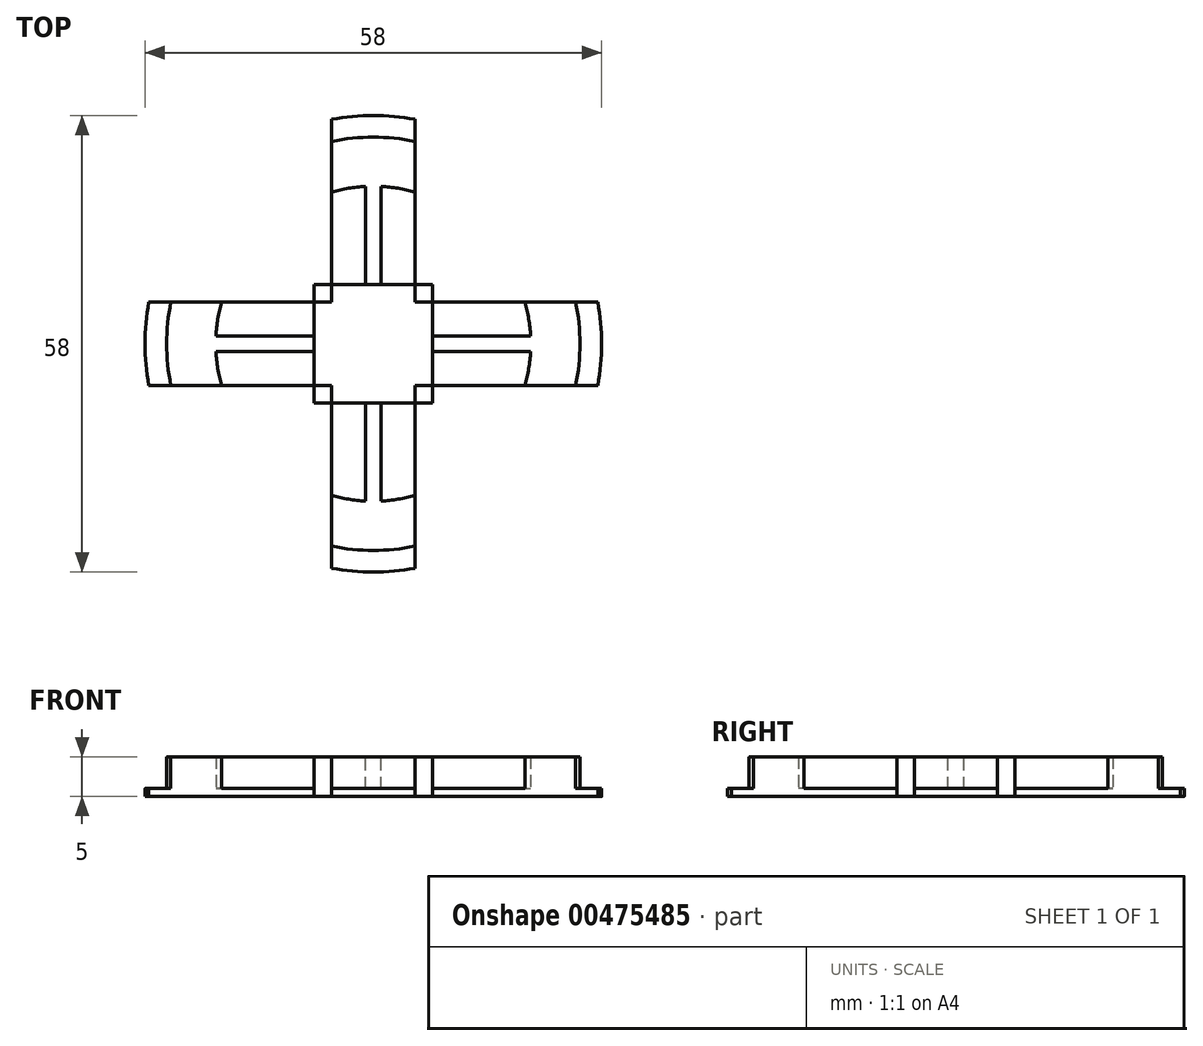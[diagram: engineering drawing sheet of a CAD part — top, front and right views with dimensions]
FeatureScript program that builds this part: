
annotation { "Feature Type Name" : "Feature", "Feature Type Description" : "" }
export const myFeature = defineFeature(function(context is Context, id is Id, definition is map)
    precondition{}
    {
        {
            var Q0;
            Q0=qCreatedBy(makeId("Top.planeOp"),FACE);
            var sketch = newSketch(context, id + "F0", { "sketchPlane" : qUnion([Q0])});
            skCircle(sketch, "E0", {"center": v(0, 0) * mm, "radius": 26.25 * mm});
            skCircle(sketch, "E1", {"center": v(0, 0) * mm, "radius": 29 * mm});
            skLineSegment(sketch, "E2.left", {"start": v(-5.27, 28.52) * mm, "end": v(-5.27, 5.27) * mm});
            skLineSegment(sketch, "E2.right", {"start": v(5.27, 28.52) * mm, "end": v(5.27, 5.27) * mm});
            skLineSegment(sketch, "E3.bottom", {"start": v(-28.52, 5.27) * mm, "end": v(-5.27, 5.27) * mm});
            skLineSegment(sketch, "E3.top", {"start": v(-28.52, -5.27) * mm, "end": v(-5.27, -5.27) * mm});
            skLineSegment(sketch, "E4.trimOffspring", {"start": v(5.27, 5.27) * mm, "end": v(28.52, 5.27) * mm});
            skLineSegment(sketch, "E5.trimOffspring", {"start": v(-5.27, -5.27) * mm, "end": v(-5.27, -28.52) * mm});
            skLineSegment(sketch, "E6.trimOffspring", {"start": v(5.27, -5.27) * mm, "end": v(28.52, -5.27) * mm});
            skLineSegment(sketch, "E7.trimOffspring", {"start": v(5.27, -5.27) * mm, "end": v(5.27, -28.52) * mm});
            skCircle(sketch, "E8", {"center": v(0, 0) * mm, "radius": 20 * mm});
            skCircle(sketch, "E9", {"center": v(0, 0) * mm, "radius": 4.1 * mm});
            skLineSegment(sketch, "E10.bottom", {"start": v(-7.5, 7.5) * mm, "end": v(7.5, 7.5) * mm});
            skLineSegment(sketch, "E10.top", {"start": v(-7.5, -7.5) * mm, "end": v(7.5, -7.5) * mm});
            skLineSegment(sketch, "E10.left", {"start": v(-7.5, 7.5) * mm, "end": v(-7.5, -7.5) * mm});
            skLineSegment(sketch, "E10.right", {"start": v(7.5, 7.5) * mm, "end": v(7.5, -7.5) * mm});
            skLineSegment(sketch, "E11.left", {"start": v(-1, 19.97) * mm, "end": v(-1, 7.5) * mm});
            skLineSegment(sketch, "E11.right", {"start": v(1, 19.97) * mm, "end": v(1, 7.5) * mm});
            skLineSegment(sketch, "E12.trimOffspring", {"start": v(-1, -7.5) * mm, "end": v(-1, -19.97) * mm});
            skLineSegment(sketch, "E13.trimOffspring", {"start": v(1, -7.5) * mm, "end": v(1, -19.97) * mm});
            skLineSegment(sketch, "E14.bottom", {"start": v(-19.97, 1) * mm, "end": v(-7.5, 1) * mm});
            skLineSegment(sketch, "E14.top", {"start": v(-19.97, -1) * mm, "end": v(-7.5, -1) * mm});
            skLineSegment(sketch, "E15.bottom", {"start": v(7.5, 1) * mm, "end": v(19.97, 1) * mm});
            skLineSegment(sketch, "E15.top", {"start": v(7.5, -1) * mm, "end": v(19.97, -1) * mm});
            skPoint(sketch, "E15.left.start.orphan", {"position": v(6.8, 1) * mm});
            skPoint(sketch, "E16.orphan", {"position": v(21.24, -1) * mm});
            skSolve(sketch);
        }
        {
            var Q0;
            {var subQ3=sQuery(id+"F0.wireOp",EDGE,"E0");var subQ9=sQuery(id+"F0.wireOp",EDGE,"E2.right");var subQ12=makeQuery(id+"F0.imprint","INTERSECT",VERTEX,{"derivedFrom":[subQ3,subQ9]});Q0=makeQuery(id+"F0.imprint","IMPRINT",FACE,{"disambiguationData":[TD([[makeQuery(id+"F0.imprint","IMPRINT",EDGE,{"disambiguationData":[TD([[subQ12,-1.0]])],"derivedFrom":subQ3}),1.0]])]});}
            var Q1;
            {var subQ0=sQuery(id+"F0.wireOp",EDGE,"E3.bottom");var subQ1=sQuery(id+"F0.wireOp",EDGE,"E0");var subQ2=makeQuery(id+"F0.imprint","INTERSECT",VERTEX,{"derivedFrom":[subQ1,subQ0]});Q1=makeQuery(id+"F0.imprint","IMPRINT",FACE,{"disambiguationData":[TD([[makeQuery(id+"F0.imprint","IMPRINT",EDGE,{"disambiguationData":[TD([[subQ2,-1.0]])],"derivedFrom":subQ1}),-1.0]])]});}
            var Q2;
            {var subQ0=sQuery(id+"F0.wireOp",EDGE,"E2.right");var subQ1=sQuery(id+"F0.wireOp",EDGE,"E0");var subQ2=makeQuery(id+"F0.imprint","INTERSECT",VERTEX,{"derivedFrom":[subQ1,subQ0]});Q2=makeQuery(id+"F0.imprint","IMPRINT",FACE,{"disambiguationData":[TD([[makeQuery(id+"F0.imprint","IMPRINT",EDGE,{"disambiguationData":[TD([[subQ2,-1.0]])],"derivedFrom":subQ1}),-1.0]])]});}
            var Q3;
            {var subQ0=sQuery(id+"F0.wireOp",EDGE,"E4.trimOffspring");var subQ1=sQuery(id+"F0.wireOp",EDGE,"E0");var subQ2=makeQuery(id+"F0.imprint","INTERSECT",VERTEX,{"derivedFrom":[subQ1,subQ0]});Q3=makeQuery(id+"F0.imprint","IMPRINT",FACE,{"disambiguationData":[TD([[makeQuery(id+"F0.imprint","IMPRINT",EDGE,{"disambiguationData":[TD([[subQ2,1.0]])],"derivedFrom":subQ1}),-1.0]])]});}
            var Q4;
            {var subQ0=sQuery(id+"F0.wireOp",EDGE,"E5.trimOffspring");var subQ1=sQuery(id+"F0.wireOp",EDGE,"E0");var subQ2=makeQuery(id+"F0.imprint","INTERSECT",VERTEX,{"derivedFrom":[subQ1,subQ0]});Q4=makeQuery(id+"F0.imprint","IMPRINT",FACE,{"disambiguationData":[TD([[makeQuery(id+"F0.imprint","IMPRINT",EDGE,{"disambiguationData":[TD([[subQ2,-1.0]])],"derivedFrom":subQ1}),-1.0]])]});}
            var Q5;
            {var subQ1=sQuery(id+"F0.wireOp",EDGE,"E3.bottom");var subQ3=sQuery(id+"F0.wireOp",EDGE,"E8");var subQ4=makeQuery(id+"F0.imprint","INTERSECT",VERTEX,{"derivedFrom":[subQ1,subQ3]});Q5=makeQuery(id+"F0.imprint","IMPRINT",FACE,{"disambiguationData":[TD([[makeQuery(id+"F0.imprint","IMPRINT",EDGE,{"disambiguationData":[TD([[subQ4,-1.0]])],"derivedFrom":subQ3}),1.0]])]});}
            var Q6;
            Q6=makeQuery(id+"F0.imprint","IMPRINT",FACE,{"disambiguationData":[TD([[makeQuery(id+"F0.imprint","IMPRINT",EDGE,{"derivedFrom":sQuery(id+"F0.wireOp",EDGE,"E9")}),-1.0]])]});
            var Q7;
            {var subQ1=sQuery(id+"F0.wireOp",EDGE,"E2.left");var subQ3=sQuery(id+"F0.wireOp",EDGE,"E8");var subQ4=makeQuery(id+"F0.imprint","INTERSECT",VERTEX,{"derivedFrom":[subQ1,subQ3]});Q7=makeQuery(id+"F0.imprint","IMPRINT",FACE,{"disambiguationData":[TD([[makeQuery(id+"F0.imprint","IMPRINT",EDGE,{"disambiguationData":[TD([[subQ4,1.0]])],"derivedFrom":subQ3}),1.0]])]});}
            var Q8;
            {var subQ1=sQuery(id+"F0.wireOp",EDGE,"E4.trimOffspring");var subQ3=sQuery(id+"F0.wireOp",EDGE,"E8");var subQ4=makeQuery(id+"F0.imprint","INTERSECT",VERTEX,{"derivedFrom":[subQ1,subQ3]});Q8=makeQuery(id+"F0.imprint","IMPRINT",FACE,{"disambiguationData":[TD([[makeQuery(id+"F0.imprint","IMPRINT",EDGE,{"disambiguationData":[TD([[subQ4,1.0]])],"derivedFrom":subQ3}),1.0]])]});}
            var Q9;
            {var subQ0=sQuery(id+"F0.wireOp",EDGE,"E4.trimOffspring");var subQ1=sQuery(id+"F0.wireOp",EDGE,"E0");var subQ2=makeQuery(id+"F0.imprint","INTERSECT",VERTEX,{"derivedFrom":[subQ1,subQ0]});Q9=makeQuery(id+"F0.imprint","IMPRINT",FACE,{"disambiguationData":[TD([[makeQuery(id+"F0.imprint","IMPRINT",EDGE,{"disambiguationData":[TD([[subQ2,1.0]])],"derivedFrom":subQ1}),1.0]])]});}
            var Q10;
            {var subQ1=sQuery(id+"F0.wireOp",EDGE,"E5.trimOffspring");var subQ3=sQuery(id+"F0.wireOp",EDGE,"E8");var subQ4=makeQuery(id+"F0.imprint","INTERSECT",VERTEX,{"derivedFrom":[subQ1,subQ3]});Q10=makeQuery(id+"F0.imprint","IMPRINT",FACE,{"disambiguationData":[TD([[makeQuery(id+"F0.imprint","IMPRINT",EDGE,{"disambiguationData":[TD([[subQ4,-1.0]])],"derivedFrom":subQ3}),1.0]])]});}
            var Q11;
            {var subQ0=sQuery(id+"F0.wireOp",EDGE,"E5.trimOffspring");var subQ1=sQuery(id+"F0.wireOp",EDGE,"E0");var subQ2=makeQuery(id+"F0.imprint","INTERSECT",VERTEX,{"derivedFrom":[subQ1,subQ0]});Q11=makeQuery(id+"F0.imprint","IMPRINT",FACE,{"disambiguationData":[TD([[makeQuery(id+"F0.imprint","IMPRINT",EDGE,{"disambiguationData":[TD([[subQ2,-1.0]])],"derivedFrom":subQ1}),1.0]])]});}
            var Q12;
            {var subQ0=sQuery(id+"F0.wireOp",EDGE,"E3.bottom");var subQ1=sQuery(id+"F0.wireOp",EDGE,"E0");var subQ2=makeQuery(id+"F0.imprint","INTERSECT",VERTEX,{"derivedFrom":[subQ1,subQ0]});Q12=makeQuery(id+"F0.imprint","IMPRINT",FACE,{"disambiguationData":[TD([[makeQuery(id+"F0.imprint","IMPRINT",EDGE,{"disambiguationData":[TD([[subQ2,-1.0]])],"derivedFrom":subQ1}),1.0]])]});}
            var Q13;
            {var subQ0=sQuery(id+"F0.wireOp",EDGE,"E3.bottom");var subQ1=sQuery(id+"F0.wireOp",EDGE,"E2.left");var subQ2=makeQuery(id+"F0.imprint","INTERSECT",VERTEX,{"derivedFrom":[subQ1,subQ0]});Q13=makeQuery(id+"F0.imprint","IMPRINT",FACE,{"disambiguationData":[TD([[makeQuery(id+"F0.imprint","IMPRINT",EDGE,{"disambiguationData":[TD([[subQ2,1.0]])],"derivedFrom":subQ1}),-1.0]])]});}
            var Q14;
            {var subQ0=sQuery(id+"F0.wireOp",EDGE,"E5.trimOffspring");var subQ1=sQuery(id+"F0.wireOp",EDGE,"E3.top");var subQ2=makeQuery(id+"F0.imprint","INTERSECT",VERTEX,{"derivedFrom":[subQ1,subQ0]});Q14=makeQuery(id+"F0.imprint","IMPRINT",FACE,{"disambiguationData":[TD([[makeQuery(id+"F0.imprint","IMPRINT",EDGE,{"disambiguationData":[TD([[subQ2,1.0]])],"derivedFrom":subQ1}),-1.0]])]});}
            var Q15;
            {var subQ0=sQuery(id+"F0.wireOp",EDGE,"E7.trimOffspring");var subQ1=sQuery(id+"F0.wireOp",EDGE,"E6.trimOffspring");var subQ2=makeQuery(id+"F0.imprint","INTERSECT",VERTEX,{"derivedFrom":[subQ1,subQ0]});Q15=makeQuery(id+"F0.imprint","IMPRINT",FACE,{"disambiguationData":[TD([[makeQuery(id+"F0.imprint","IMPRINT",EDGE,{"disambiguationData":[TD([[subQ2,-1.0]])],"derivedFrom":subQ1}),-1.0]])]});}
            var Q16;
            {var subQ0=sQuery(id+"F0.wireOp",EDGE,"E4.trimOffspring");var subQ1=sQuery(id+"F0.wireOp",EDGE,"E2.right");var subQ2=makeQuery(id+"F0.imprint","INTERSECT",VERTEX,{"derivedFrom":[subQ1,subQ0]});Q16=makeQuery(id+"F0.imprint","IMPRINT",FACE,{"disambiguationData":[TD([[makeQuery(id+"F0.imprint","IMPRINT",EDGE,{"disambiguationData":[TD([[subQ2,1.0]])],"derivedFrom":subQ1}),1.0]])]});}
            var Q17;
            {var subQ0=sQuery(id+"F0.wireOp",EDGE,"E15.bottom");Q17=makeQuery(id+"F0.imprint","IMPRINT",FACE,{"disambiguationData":[TD([[makeQuery(id+"F0.imprint","IMPRINT",EDGE,{"derivedFrom":subQ0}),-1.0]])]});}
            var Q18;
            {var subQ5=sQuery(id+"F0.wireOp",EDGE,"E15.top");Q18=makeQuery(id+"F0.imprint","IMPRINT",FACE,{"disambiguationData":[TD([[makeQuery(id+"F0.imprint","IMPRINT",EDGE,{"derivedFrom":subQ5}),-1.0]])]});}
            var Q19;
            {var subQ5=sQuery(id+"F0.wireOp",EDGE,"E14.top");Q19=makeQuery(id+"F0.imprint","IMPRINT",FACE,{"disambiguationData":[TD([[makeQuery(id+"F0.imprint","IMPRINT",EDGE,{"derivedFrom":subQ5}),-1.0]])]});}
            var Q20;
            {var subQ0=sQuery(id+"F0.wireOp",EDGE,"E14.bottom");Q20=makeQuery(id+"F0.imprint","IMPRINT",FACE,{"disambiguationData":[TD([[makeQuery(id+"F0.imprint","IMPRINT",EDGE,{"derivedFrom":subQ0}),-1.0]])]});}
            var Q21;
            {var subQ0=sQuery(id+"F0.wireOp",EDGE,"E11.left");Q21=makeQuery(id+"F0.imprint","IMPRINT",FACE,{"disambiguationData":[TD([[makeQuery(id+"F0.imprint","IMPRINT",EDGE,{"derivedFrom":subQ0}),1.0]])]});}
            var Q22;
            {var subQ5=sQuery(id+"F0.wireOp",EDGE,"E11.right");Q22=makeQuery(id+"F0.imprint","IMPRINT",FACE,{"disambiguationData":[TD([[makeQuery(id+"F0.imprint","IMPRINT",EDGE,{"derivedFrom":subQ5}),1.0]])]});}
            var Q23;
            {var subQ5=sQuery(id+"F0.wireOp",EDGE,"E13.trimOffspring");Q23=makeQuery(id+"F0.imprint","IMPRINT",FACE,{"disambiguationData":[TD([[makeQuery(id+"F0.imprint","IMPRINT",EDGE,{"derivedFrom":subQ5}),1.0]])]});}
            var Q24;
            {var subQ0=sQuery(id+"F0.wireOp",EDGE,"E12.trimOffspring");Q24=makeQuery(id+"F0.imprint","IMPRINT",FACE,{"disambiguationData":[TD([[makeQuery(id+"F0.imprint","IMPRINT",EDGE,{"derivedFrom":subQ0}),1.0]])]});}
            extrude(context, id + "F1", {"entities" : qUnion([Q0, Q1, Q2, Q3, Q4, Q5, Q6, Q7, Q8, Q9, Q10, Q11, Q12, Q13, Q14, Q15, Q16, Q17, Q18, Q19, Q20, Q21, Q22, Q23, Q24]), "oppositeDirection" : true, "depth" : 1 * mm, "offsetDistance" : 25 * mm});
        }
        {
            var Q0;
            {var subQ0=sQuery(id+"F0.wireOp",EDGE,"E4.trimOffspring");var subQ1=sQuery(id+"F0.wireOp",EDGE,"E0");var subQ2=makeQuery(id+"F0.imprint","INTERSECT",VERTEX,{"derivedFrom":[subQ1,subQ0]});Q0=makeQuery(id+"F0.imprint","IMPRINT",FACE,{"disambiguationData":[TD([[makeQuery(id+"F0.imprint","IMPRINT",EDGE,{"disambiguationData":[TD([[subQ2,1.0]])],"derivedFrom":subQ1}),1.0]])]});}
            var Q1;
            {var subQ0=sQuery(id+"F0.wireOp",EDGE,"E2.right");var subQ1=sQuery(id+"F0.wireOp",EDGE,"E0");var subQ2=makeQuery(id+"F0.imprint","INTERSECT",VERTEX,{"derivedFrom":[subQ1,subQ0]});Q1=makeQuery(id+"F0.imprint","IMPRINT",FACE,{"disambiguationData":[TD([[makeQuery(id+"F0.imprint","IMPRINT",EDGE,{"disambiguationData":[TD([[subQ2,-1.0]])],"derivedFrom":subQ1}),1.0]])]});}
            var Q2;
            {var subQ0=sQuery(id+"F0.wireOp",EDGE,"E3.bottom");var subQ1=sQuery(id+"F0.wireOp",EDGE,"E0");var subQ2=makeQuery(id+"F0.imprint","INTERSECT",VERTEX,{"derivedFrom":[subQ1,subQ0]});Q2=makeQuery(id+"F0.imprint","IMPRINT",FACE,{"disambiguationData":[TD([[makeQuery(id+"F0.imprint","IMPRINT",EDGE,{"disambiguationData":[TD([[subQ2,-1.0]])],"derivedFrom":subQ1}),1.0]])]});}
            var Q3;
            {var subQ0=sQuery(id+"F0.wireOp",EDGE,"E5.trimOffspring");var subQ1=sQuery(id+"F0.wireOp",EDGE,"E0");var subQ2=makeQuery(id+"F0.imprint","INTERSECT",VERTEX,{"derivedFrom":[subQ1,subQ0]});Q3=makeQuery(id+"F0.imprint","IMPRINT",FACE,{"disambiguationData":[TD([[makeQuery(id+"F0.imprint","IMPRINT",EDGE,{"disambiguationData":[TD([[subQ2,-1.0]])],"derivedFrom":subQ1}),1.0]])]});}
            var Q4;
            {var subQ0=sQuery(id+"F0.wireOp",EDGE,"E11.left");Q4=makeQuery(id+"F0.imprint","IMPRINT",FACE,{"disambiguationData":[TD([[makeQuery(id+"F0.imprint","IMPRINT",EDGE,{"derivedFrom":subQ0}),1.0]])]});}
            var Q5;
            {var subQ0=sQuery(id+"F0.wireOp",EDGE,"E14.bottom");Q5=makeQuery(id+"F0.imprint","IMPRINT",FACE,{"disambiguationData":[TD([[makeQuery(id+"F0.imprint","IMPRINT",EDGE,{"derivedFrom":subQ0}),-1.0]])]});}
            var Q6;
            {var subQ0=sQuery(id+"F0.wireOp",EDGE,"E15.bottom");Q6=makeQuery(id+"F0.imprint","IMPRINT",FACE,{"disambiguationData":[TD([[makeQuery(id+"F0.imprint","IMPRINT",EDGE,{"derivedFrom":subQ0}),-1.0]])]});}
            var Q7;
            {var subQ0=sQuery(id+"F0.wireOp",EDGE,"E12.trimOffspring");Q7=makeQuery(id+"F0.imprint","IMPRINT",FACE,{"disambiguationData":[TD([[makeQuery(id+"F0.imprint","IMPRINT",EDGE,{"derivedFrom":subQ0}),1.0]])]});}
            var Q8;
            Q8=makeQuery(id+"F0.imprint","IMPRINT",FACE,{"disambiguationData":[TD([[makeQuery(id+"F0.imprint","IMPRINT",EDGE,{"derivedFrom":sQuery(id+"F0.wireOp",EDGE,"E9")}),-1.0]])]});
            var Q9;
            {var subQ0=sQuery(id+"F0.wireOp",EDGE,"E3.bottom");var subQ1=sQuery(id+"F0.wireOp",EDGE,"E2.left");var subQ2=makeQuery(id+"F0.imprint","INTERSECT",VERTEX,{"derivedFrom":[subQ1,subQ0]});Q9=makeQuery(id+"F0.imprint","IMPRINT",FACE,{"disambiguationData":[TD([[makeQuery(id+"F0.imprint","IMPRINT",EDGE,{"disambiguationData":[TD([[subQ2,1.0]])],"derivedFrom":subQ1}),-1.0]])]});}
            var Q10;
            {var subQ0=sQuery(id+"F0.wireOp",EDGE,"E5.trimOffspring");var subQ1=sQuery(id+"F0.wireOp",EDGE,"E3.top");var subQ2=makeQuery(id+"F0.imprint","INTERSECT",VERTEX,{"derivedFrom":[subQ1,subQ0]});Q10=makeQuery(id+"F0.imprint","IMPRINT",FACE,{"disambiguationData":[TD([[makeQuery(id+"F0.imprint","IMPRINT",EDGE,{"disambiguationData":[TD([[subQ2,1.0]])],"derivedFrom":subQ1}),-1.0]])]});}
            var Q11;
            {var subQ0=sQuery(id+"F0.wireOp",EDGE,"E7.trimOffspring");var subQ1=sQuery(id+"F0.wireOp",EDGE,"E6.trimOffspring");var subQ2=makeQuery(id+"F0.imprint","INTERSECT",VERTEX,{"derivedFrom":[subQ1,subQ0]});Q11=makeQuery(id+"F0.imprint","IMPRINT",FACE,{"disambiguationData":[TD([[makeQuery(id+"F0.imprint","IMPRINT",EDGE,{"disambiguationData":[TD([[subQ2,-1.0]])],"derivedFrom":subQ1}),-1.0]])]});}
            var Q12;
            {var subQ0=sQuery(id+"F0.wireOp",EDGE,"E4.trimOffspring");var subQ1=sQuery(id+"F0.wireOp",EDGE,"E2.right");var subQ2=makeQuery(id+"F0.imprint","INTERSECT",VERTEX,{"derivedFrom":[subQ1,subQ0]});Q12=makeQuery(id+"F0.imprint","IMPRINT",FACE,{"disambiguationData":[TD([[makeQuery(id+"F0.imprint","IMPRINT",EDGE,{"disambiguationData":[TD([[subQ2,1.0]])],"derivedFrom":subQ1}),1.0]])]});}
            extrude(context, id + "F2", {"entities" : qUnion([Q0, Q1, Q2, Q3, Q4, Q5, Q6, Q7, Q8, Q9, Q10, Q11, Q12]), "operationType" : NewBodyOperationType.ADD, "depth" : 4 * mm, "offsetDistance" : 25 * mm});
        }
    });
